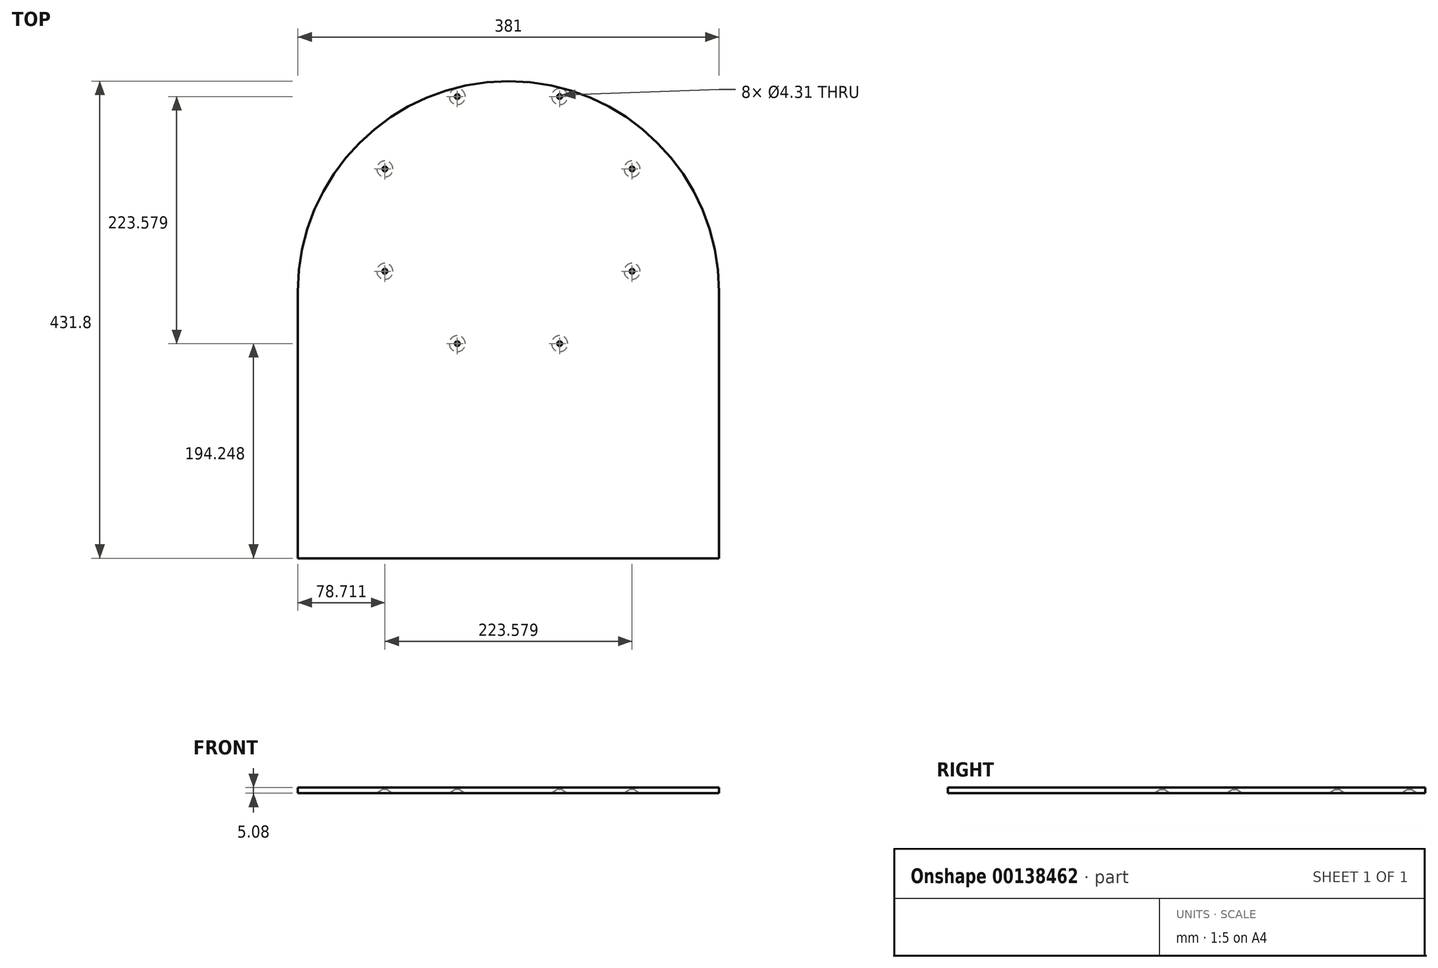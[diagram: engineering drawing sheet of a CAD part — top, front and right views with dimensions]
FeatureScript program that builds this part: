
annotation { "Feature Type Name" : "Feature", "Feature Type Description" : "" }
export const myFeature = defineFeature(function(context is Context, id is Id, definition is map)
    precondition{}
    {
        {
            var Q0;
            Q0=qCreatedBy(makeId("Top.planeOp"),FACE);
            var sketch = newSketch(context, id + "F0", { "sketchPlane" : qUnion([Q0])});
            skLineSegment(sketch, "E0.bottom", {"start": v(0, 0) * mm, "end": v(381, 0) * mm, "construction": true});
            skLineSegment(sketch, "E0.top", {"start": v(0, -241.3) * mm, "end": v(381, -241.3) * mm});
            skLineSegment(sketch, "E0.left", {"start": v(0, 0) * mm, "end": v(0, -241.3) * mm});
            skLineSegment(sketch, "E0.right", {"start": v(381, 0) * mm, "end": v(381, -241.3) * mm});
            skArc(sketch, "E1", {"start": v(381, 0) * mm, "mid": v(190.5, 190.5) * mm, "end": v(0, 0) * mm});
            skCircle(sketch, "E2", {"center": v(190.5, 64.74) * mm, "radius": 125.76 * mm, "construction": true});
            skLineSegment(sketch, "E3", {"start": v(190.5, 64.74) * mm, "end": v(190.5, 0) * mm, "construction": true});
            skCircle(sketch, "E4.cCircle", {"center": v(190.5, 64.74) * mm, "radius": 111.79 * mm, "construction": true});
            skLineSegment(sketch, "E4.0", {"start": v(144.2, 176.53) * mm, "end": v(236.8, 176.53) * mm, "construction": true});
            skLineSegment(sketch, "E4.1", {"start": v(236.8, 176.53) * mm, "end": v(302.29, 111.04) * mm, "construction": true});
            skLineSegment(sketch, "E4.2", {"start": v(302.29, 111.04) * mm, "end": v(302.29, 18.43) * mm, "construction": true});
            skLineSegment(sketch, "E4.3", {"start": v(302.29, 18.43) * mm, "end": v(236.8, -47.05) * mm, "construction": true});
            skLineSegment(sketch, "E4.4", {"start": v(236.8, -47.05) * mm, "end": v(144.2, -47.05) * mm, "construction": true});
            skLineSegment(sketch, "E4.5", {"start": v(144.2, -47.05) * mm, "end": v(78.71, 18.43) * mm, "construction": true});
            skLineSegment(sketch, "E4.6", {"start": v(78.71, 18.43) * mm, "end": v(78.71, 111.04) * mm, "construction": true});
            skLineSegment(sketch, "E4.7", {"start": v(78.71, 111.04) * mm, "end": v(144.2, 176.53) * mm, "construction": true});
            skPoint(sketch, "E4.0.midPoint", {"position": v(190.5, 176.53) * mm});
            skCircle(sketch, "E5", {"center": v(144.2, 176.53) * mm, "radius": 4.76 * mm, "construction": true});
            skCircle(sketch, "E6", {"center": v(144.2, 176.53) * mm, "radius": 2.15 * mm});
            skCircle(sketch, "E7", {"center": v(236.8, 176.53) * mm, "radius": 2.15 * mm});
            skCircle(sketch, "E8", {"center": v(302.29, 111.04) * mm, "radius": 2.15 * mm});
            skCircle(sketch, "E9", {"center": v(302.29, 18.43) * mm, "radius": 2.15 * mm});
            skCircle(sketch, "E10", {"center": v(236.8, -47.05) * mm, "radius": 2.15 * mm});
            skCircle(sketch, "E11", {"center": v(144.2, -47.05) * mm, "radius": 2.15 * mm});
            skCircle(sketch, "E12", {"center": v(78.71, 18.43) * mm, "radius": 2.15 * mm});
            skCircle(sketch, "E13", {"center": v(78.71, 111.04) * mm, "radius": 2.15 * mm});
            skSolve(sketch);
        }
        {
            var Q0;
            Q0 = qSketchRegion(id + "F0", true);
            extrude(context, id + "F1", {"entities" : qUnion([Q0]), "depth" : 5.08 * mm});
        }
        {
            var Q0;
            Q0=makeQuery(id+"F1.opExtrude","CAP_EDGE",EDGE,{"disambiguationData":[OSD([sQuery(id+"F0.wireOp",EDGE,"E10")])],"isStart":true});
            var Q1;
            Q1=makeQuery(id+"F1.opExtrude","CAP_EDGE",EDGE,{"disambiguationData":[OSD([sQuery(id+"F0.wireOp",EDGE,"E9")])],"isStart":true});
            var Q2;
            Q2=makeQuery(id+"F1.opExtrude","CAP_EDGE",EDGE,{"disambiguationData":[OSD([sQuery(id+"F0.wireOp",EDGE,"E8")])],"isStart":true});
            var Q3;
            Q3=makeQuery(id+"F1.opExtrude","CAP_EDGE",EDGE,{"disambiguationData":[OSD([sQuery(id+"F0.wireOp",EDGE,"E11")])],"isStart":true});
            var Q4;
            Q4=makeQuery(id+"F1.opExtrude","CAP_EDGE",EDGE,{"disambiguationData":[OSD([sQuery(id+"F0.wireOp",EDGE,"E12")])],"isStart":true});
            var Q5;
            Q5=makeQuery(id+"F1.opExtrude","CAP_EDGE",EDGE,{"disambiguationData":[OSD([sQuery(id+"F0.wireOp",EDGE,"E13")])],"isStart":true});
            var Q6;
            Q6=makeQuery(id+"F1.opExtrude","CAP_EDGE",EDGE,{"disambiguationData":[OSD([sQuery(id+"F0.wireOp",EDGE,"E6")])],"isStart":true});
            var Q7;
            Q7=makeQuery(id+"F1.opExtrude","CAP_EDGE",EDGE,{"disambiguationData":[OSD([sQuery(id+"F0.wireOp",EDGE,"E7")])],"isStart":true});
            chamfer(context, id + "F2", {"entities" : qUnion([Q0, Q1, Q2, Q3, Q4, Q5, Q6, Q7]), "chamferType" : ChamferType.TWO_OFFSETS, "width1" : 5.08 * mm, "oppositeDirection" : false, "width2" : 3.17 * mm, "tangentPropagation" : true});
        }
    });
